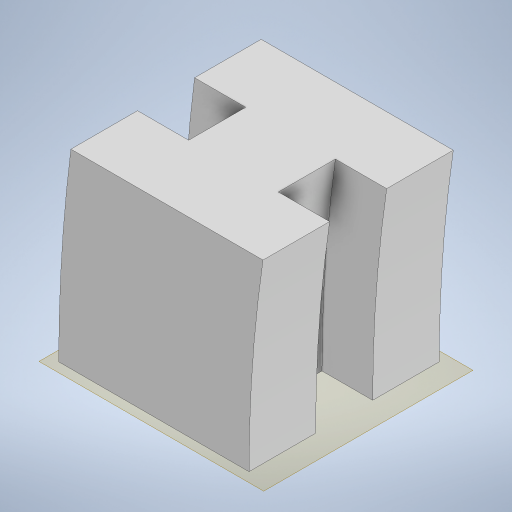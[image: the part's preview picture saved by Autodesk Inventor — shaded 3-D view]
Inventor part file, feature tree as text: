
AUTODESK INVENTOR PART (.ipt)
format: ipt  version: 2023 (Build 270158000, 158)  size: 272,896 bytes
history: native  units: mm
features: sketch x3, sweep x1, extrude x1
ambient origin geometry x8: Origin, YZ Plane, XZ Plane, XY Plane, X Axis, Y Axis, Z Axis, Center Point
bodies: Solid1 (feature_tree)
feature tree (5):
  sweep  "Sweep1"
  extrude  "Extrusion2"  Depth=9.0mm
  sketch  "Sketch1"  dims[d1=440.0mm d5=100.0mm]
  sketch  "Sketch2"  dims[d17=220.0mm d18=9.0mm]
  sketch  "Sketch4"  dims[d19=8.0mm d21=14.0mm d22=30.0mm d23=15.0mm d24=4.5mm d25=7.0mm d26=0.0mm d27=0.0mm d34=469.425714mm d35=30.0mm d36=50.803636mm d37=269.071113mm d38=0.0mm d39=0.0mm]
